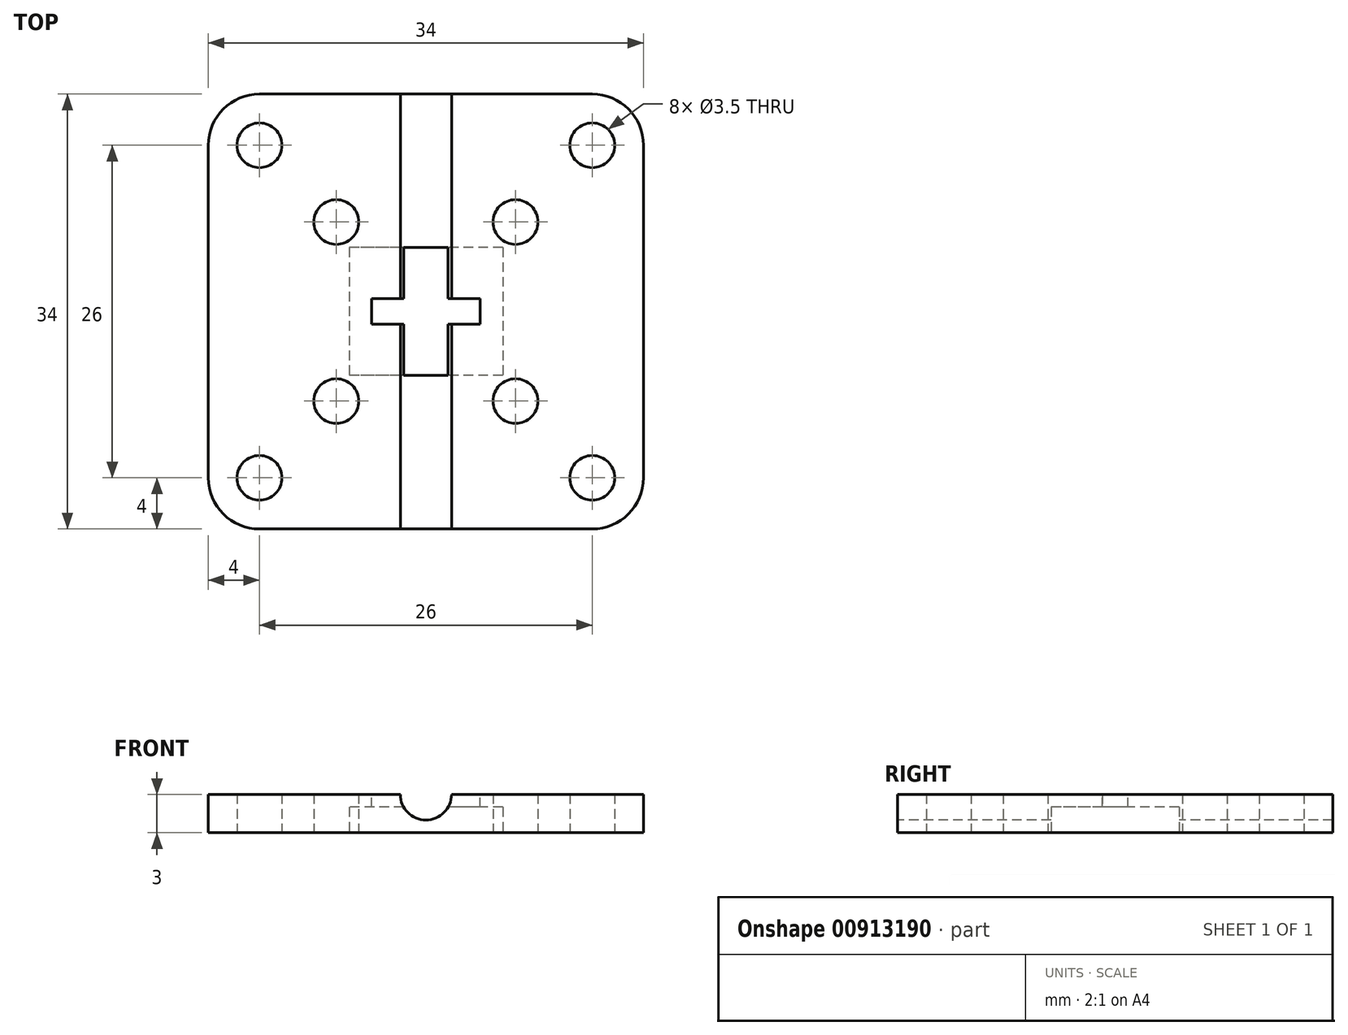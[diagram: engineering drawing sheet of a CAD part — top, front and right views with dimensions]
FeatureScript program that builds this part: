
annotation { "Feature Type Name" : "Feature", "Feature Type Description" : "" }
export const myFeature = defineFeature(function(context is Context, id is Id, definition is map)
    precondition{}
    {
        {
            var Q0;
            Q0=qCreatedBy(makeId("Top.planeOp"),FACE);
            var sketch = newSketch(context, id + "F0", { "sketchPlane" : qUnion([Q0])});
            skCircle(sketch, "E0", {"center": v(-7, 7) * mm, "radius": 1.75 * mm});
            skCircle(sketch, "E1", {"center": v(7, 7) * mm, "radius": 1.75 * mm});
            skCircle(sketch, "E2", {"center": v(7, -7) * mm, "radius": 1.75 * mm});
            skCircle(sketch, "E3", {"center": v(-7, -7) * mm, "radius": 1.75 * mm});
            skCircle(sketch, "E4", {"center": v(13, 13) * mm, "radius": 1.75 * mm});
            skCircle(sketch, "E5", {"center": v(-13, 13) * mm, "radius": 1.75 * mm});
            skCircle(sketch, "E6", {"center": v(-13, -13) * mm, "radius": 1.75 * mm});
            skCircle(sketch, "E7", {"center": v(13, -13) * mm, "radius": 1.75 * mm});
            skArc(sketch, "E8", {"start": v(-13, -17) * mm, "mid": v(-15.83, -15.83) * mm, "end": v(-17, -13) * mm});
            skArc(sketch, "E9", {"start": v(-17, 13) * mm, "mid": v(-15.83, 15.83) * mm, "end": v(-13, 17) * mm});
            skArc(sketch, "E10", {"start": v(13, 17) * mm, "mid": v(15.83, 15.83) * mm, "end": v(17, 13) * mm});
            skArc(sketch, "E11", {"start": v(17, -13) * mm, "mid": v(15.83, -15.83) * mm, "end": v(13, -17) * mm});
            skLineSegment(sketch, "E12", {"start": v(-17, -13) * mm, "end": v(-17, 13) * mm});
            skLineSegment(sketch, "E13", {"start": v(-13, 17) * mm, "end": v(13, 17) * mm});
            skLineSegment(sketch, "E14", {"start": v(17, 13) * mm, "end": v(17, -13) * mm});
            skLineSegment(sketch, "E15", {"start": v(13, -17) * mm, "end": v(-13, -17) * mm});
            skLineSegment(sketch, "E16.bottom", {"start": v(6, 5) * mm, "end": v(-6, 5) * mm});
            skLineSegment(sketch, "E16.top", {"start": v(6, -5) * mm, "end": v(-6, -5) * mm});
            skLineSegment(sketch, "E16.left", {"start": v(6, 5) * mm, "end": v(6, -5) * mm});
            skLineSegment(sketch, "E16.right", {"start": v(-6, 5) * mm, "end": v(-6, -5) * mm});
            skPoint(sketch, "E16.middle", {"position": v(0, 0) * mm});
            skSolve(sketch);
        }
        {
            var Q0;
            Q0=qSketchRegion(id+"F0",true);
            extrude(context, id + "F1", {"entities" : qUnion([Q0]), "depth" : 2 * mm, "offsetDistance" : 25 * mm});
        }
        {
            var Q0;
            Q0=makeQuery(id+"F1.opExtrude","CAP_FACE",FACE,{"disambiguationData":[OSD([sQuery(id+"F0.wireOp",EDGE,"E0"),sQuery(id+"F0.wireOp",EDGE,"E1"),sQuery(id+"F0.wireOp",EDGE,"E2"),sQuery(id+"F0.wireOp",EDGE,"E3"),sQuery(id+"F0.wireOp",EDGE,"E4"),sQuery(id+"F0.wireOp",EDGE,"E5"),sQuery(id+"F0.wireOp",EDGE,"E6"),sQuery(id+"F0.wireOp",EDGE,"E7"),sQuery(id+"F0.wireOp",EDGE,"E8"),sQuery(id+"F0.wireOp",EDGE,"E9"),sQuery(id+"F0.wireOp",EDGE,"E10"),sQuery(id+"F0.wireOp",EDGE,"E11"),sQuery(id+"F0.wireOp",EDGE,"E12"),sQuery(id+"F0.wireOp",EDGE,"E13"),sQuery(id+"F0.wireOp",EDGE,"E14"),sQuery(id+"F0.wireOp",EDGE,"E15"),sQuery(id+"F0.wireOp",EDGE,"E16.bottom"),sQuery(id+"F0.wireOp",EDGE,"E16.top"),sQuery(id+"F0.wireOp",EDGE,"E16.left"),sQuery(id+"F0.wireOp",EDGE,"E16.right")])],"isStart":false});
            var sketch = newSketch(context, id + "F2", { "sketchPlane" : qUnion([Q0])});
            skCircle(sketch, "E17", {"center": v(-7, 7) * mm, "radius": 1.75 * mm});
            skCircle(sketch, "E18", {"center": v(7, -7) * mm, "radius": 1.75 * mm});
            skCircle(sketch, "E19", {"center": v(-7, -7) * mm, "radius": 1.75 * mm});
            skCircle(sketch, "E20", {"center": v(-13, -13) * mm, "radius": 1.75 * mm});
            skCircle(sketch, "E21", {"center": v(-13, 13) * mm, "radius": 1.75 * mm});
            skCircle(sketch, "E22", {"center": v(13, 13) * mm, "radius": 1.75 * mm});
            skCircle(sketch, "E23", {"center": v(13, -13) * mm, "radius": 1.75 * mm});
            skCircle(sketch, "E24", {"center": v(7, 7) * mm, "radius": 1.75 * mm});
            skArc(sketch, "E25", {"start": v(-13, -17) * mm, "mid": v(-15.83, -15.83) * mm, "end": v(-17, -13) * mm});
            skArc(sketch, "E26", {"start": v(-17, 13) * mm, "mid": v(-15.83, 15.83) * mm, "end": v(-13, 17) * mm});
            skArc(sketch, "E27", {"start": v(13, 17) * mm, "mid": v(15.83, 15.83) * mm, "end": v(17, 13) * mm});
            skArc(sketch, "E28", {"start": v(17, -13) * mm, "mid": v(15.83, -15.83) * mm, "end": v(13, -17) * mm});
            skLineSegment(sketch, "E29", {"start": v(-17, -13) * mm, "end": v(-17, 13) * mm});
            skLineSegment(sketch, "E30", {"start": v(-13, 17) * mm, "end": v(13, 17) * mm});
            skLineSegment(sketch, "E31", {"start": v(17, 13) * mm, "end": v(17, -13) * mm});
            skLineSegment(sketch, "E32", {"start": v(13, -17) * mm, "end": v(-13, -17) * mm});
            skSolve(sketch);
        }
        {
            var Q0;
            Q0=qSketchRegion(id+"F2",true);
            extrude(context, id + "F3", {"entities" : qUnion([Q0]), "operationType" : NewBodyOperationType.ADD, "depth" : 1 * mm, "offsetDistance" : 25 * mm});
        }
        {
            var Q0;
            Q0=makeQuery(id+"F3.boolean.opBoolean","MERGE",FACE,{"derivedFrom":[makeQuery(id+"F1.opExtrude","SWEPT_FACE",FACE,{"disambiguationData":[OSD([sQuery(id+"F0.wireOp",EDGE,"E15")])]}),makeQuery(id+"F3.opExtrude","SWEPT_FACE",FACE,{"disambiguationData":[OSD([sQuery(id+"F2.wireOp",EDGE,"E32")])]})]});
            var sketch = newSketch(context, id + "F4", { "sketchPlane" : qUnion([Q0])});
            skCircle(sketch, "E33", {"center": v(0, 3) * mm, "radius": 2 * mm});
            skSolve(sketch);
        }
        {
            var Q0;
            Q0=qSketchRegion(id+"F4",true);
            extrude(context, id + "F5", {"entities" : qUnion([Q0]), "depth" : -34 * mm, "offsetDistance" : 25 * mm});
        }
        {
            var Q0;
            Q0=makeQuery(id+"F3.opExtrude","CAP_FACE",FACE,{"disambiguationData":[OSD([sQuery(id+"F2.wireOp",EDGE,"E17"),sQuery(id+"F2.wireOp",EDGE,"E18"),sQuery(id+"F2.wireOp",EDGE,"E19"),sQuery(id+"F2.wireOp",EDGE,"E20"),sQuery(id+"F2.wireOp",EDGE,"E21"),sQuery(id+"F2.wireOp",EDGE,"E22"),sQuery(id+"F2.wireOp",EDGE,"E23"),sQuery(id+"F2.wireOp",EDGE,"E24"),sQuery(id+"F2.wireOp",EDGE,"E25"),sQuery(id+"F2.wireOp",EDGE,"E26"),sQuery(id+"F2.wireOp",EDGE,"E27"),sQuery(id+"F2.wireOp",EDGE,"E28"),sQuery(id+"F2.wireOp",EDGE,"E29"),sQuery(id+"F2.wireOp",EDGE,"E30"),sQuery(id+"F2.wireOp",EDGE,"E31"),sQuery(id+"F2.wireOp",EDGE,"E32")])],"isStart":false});
            var sketch = newSketch(context, id + "F6", { "sketchPlane" : qUnion([Q0])});
            skLineSegment(sketch, "E34.bottom", {"start": v(4.25, 1) * mm, "end": v(-4.25, 1) * mm});
            skLineSegment(sketch, "E34.top", {"start": v(4.25, -1) * mm, "end": v(-4.25, -1) * mm});
            skLineSegment(sketch, "E34.left", {"start": v(4.25, 1) * mm, "end": v(4.25, -1) * mm});
            skLineSegment(sketch, "E34.right", {"start": v(-4.25, 1) * mm, "end": v(-4.25, -1) * mm});
            skPoint(sketch, "E34.middle", {"position": v(0, 0) * mm});
            skSolve(sketch);
        }
        {
            var Q0;
            Q0=qSketchRegion(id+"F6",true);
            extrude(context, id + "F7", {"entities" : qUnion([Q0]), "depth" : -5 * mm, "offsetDistance" : 25 * mm});
        }
        {
            var Q0;
            Q0=makeQuery(id+"F5.opExtrude","SWEPT_BODY",BODY,{"disambiguationData":[OSD([sQuery(id+"F4.wireOp",EDGE,"E33")])]});
            var Q1;
            Q1=makeQuery(id+"F7.opExtrude","SWEPT_BODY",BODY,{"disambiguationData":[OSD([sQuery(id+"F6.wireOp",EDGE,"E34.bottom"),sQuery(id+"F6.wireOp",EDGE,"E34.top"),sQuery(id+"F6.wireOp",EDGE,"E34.left"),sQuery(id+"F6.wireOp",EDGE,"E34.right")])]});
            var Q2;
            Q2=makeQuery(id+"F1.opExtrude","SWEPT_BODY",BODY,{"disambiguationData":[OSD([sQuery(id+"F0.wireOp",EDGE,"E0"),sQuery(id+"F0.wireOp",EDGE,"E1"),sQuery(id+"F0.wireOp",EDGE,"E2"),sQuery(id+"F0.wireOp",EDGE,"E3"),sQuery(id+"F0.wireOp",EDGE,"E4"),sQuery(id+"F0.wireOp",EDGE,"E5"),sQuery(id+"F0.wireOp",EDGE,"E6"),sQuery(id+"F0.wireOp",EDGE,"E7"),sQuery(id+"F0.wireOp",EDGE,"E8"),sQuery(id+"F0.wireOp",EDGE,"E9"),sQuery(id+"F0.wireOp",EDGE,"E10"),sQuery(id+"F0.wireOp",EDGE,"E11"),sQuery(id+"F0.wireOp",EDGE,"E12"),sQuery(id+"F0.wireOp",EDGE,"E13"),sQuery(id+"F0.wireOp",EDGE,"E14"),sQuery(id+"F0.wireOp",EDGE,"E15"),sQuery(id+"F0.wireOp",EDGE,"E16.bottom"),sQuery(id+"F0.wireOp",EDGE,"E16.top"),sQuery(id+"F0.wireOp",EDGE,"E16.left"),sQuery(id+"F0.wireOp",EDGE,"E16.right")])]});
            booleanBodies(context, id + "F8", {"operationType" : BooleanOperationType.SUBTRACTION, "tools" : qUnion([Q0, Q1]), "targets" : qUnion([Q2])});
        }
    });
